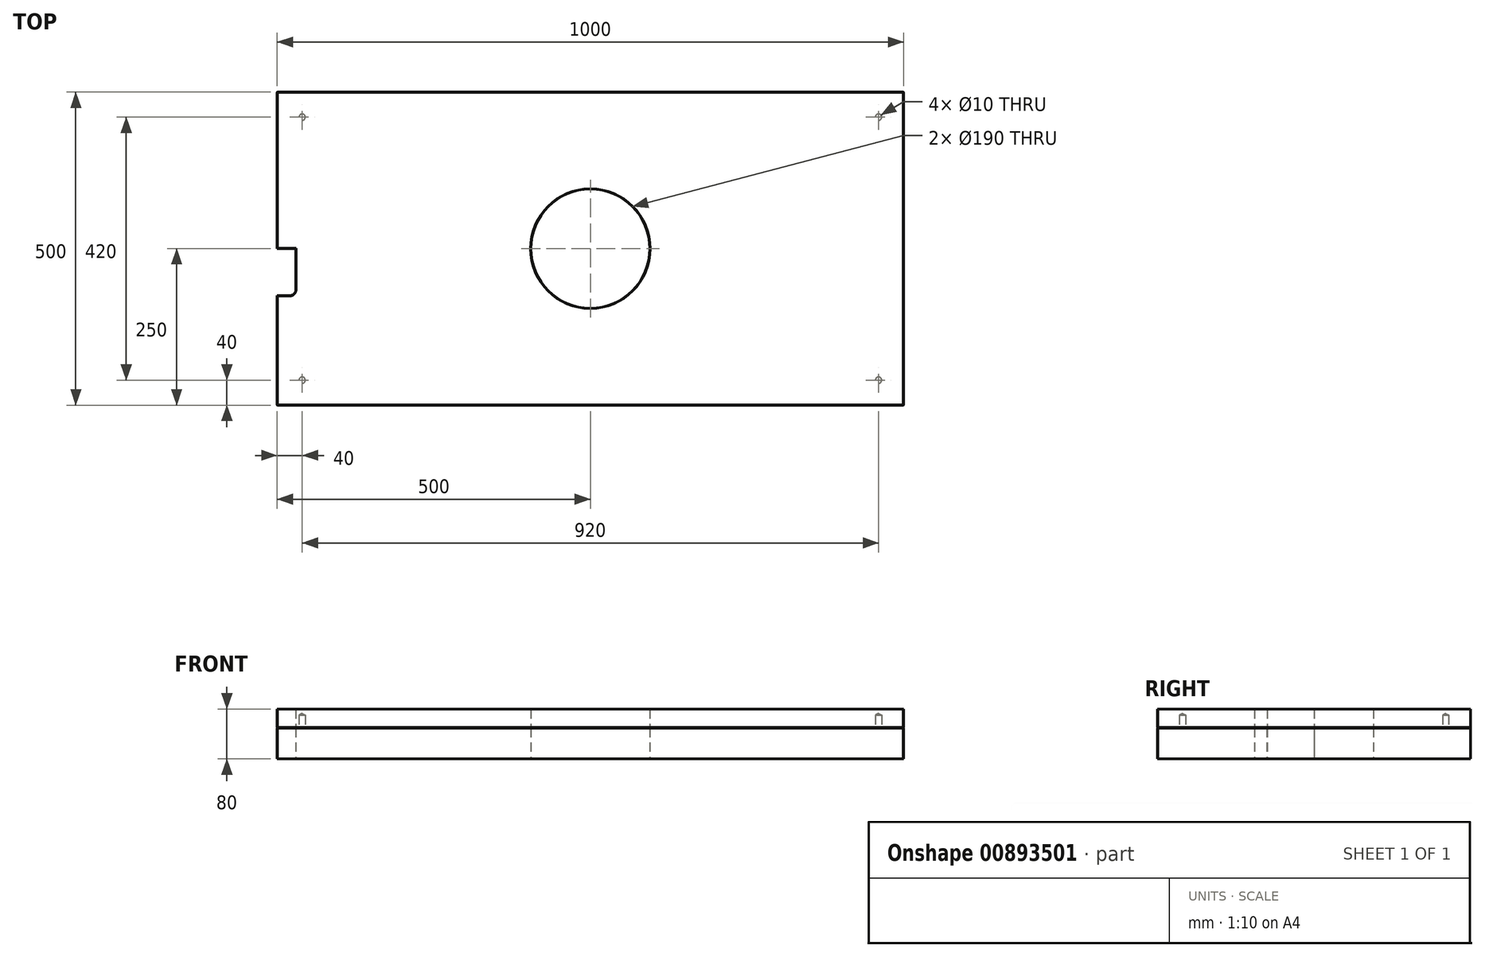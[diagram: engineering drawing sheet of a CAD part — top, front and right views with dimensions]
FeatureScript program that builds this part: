
annotation { "Feature Type Name" : "Feature", "Feature Type Description" : "" }
export const myFeature = defineFeature(function(context is Context, id is Id, definition is map)
    precondition{}
    {
        {
            var Q0;
            Q0=qCreatedBy(makeId("Top.planeOp"),FACE);
            var sketch = newSketch(context, id + "F0", { "sketchPlane" : qUnion([Q0])});
            skLineSegment(sketch, "E0", {"start": v(-650, 0) * mm, "end": v(350, 0) * mm, "construction": true});
            skLineSegment(sketch, "E1.bottom", {"start": v(350, 75) * mm, "end": v(330, 75) * mm});
            skLineSegment(sketch, "E1.top", {"start": v(350, -75) * mm, "end": v(330, -75) * mm});
            skLineSegment(sketch, "E1.left", {"start": v(350, 75) * mm, "end": v(350, -75) * mm});
            skLineSegment(sketch, "E1.right", {"start": v(320, 65) * mm, "end": v(320, -65) * mm});
            skPoint(sketch, "E2.visualSharp", {"position": v(320, -75) * mm});
            skArc(sketch, "E2.filletArc", {"start": v(320, -65) * mm, "mid": v(322.93, -72.07) * mm, "end": v(330, -75) * mm});
            skPoint(sketch, "E3.visualSharp", {"position": v(320, 75) * mm});
            skArc(sketch, "E3.filletArc", {"start": v(330, 75) * mm, "mid": v(322.93, 72.07) * mm, "end": v(320, 65) * mm});
            skLineSegment(sketch, "E4", {"start": v(-150, 250) * mm, "end": v(-150, -250) * mm, "construction": true});
            skLineSegment(sketch, "E5.MirrorCS", {"start": v(-650, 75) * mm, "end": v(-630, 75) * mm});
            skLineSegment(sketch, "E6.MirrorCS", {"start": v(-620, 65) * mm, "end": v(-620, -65) * mm});
            skArc(sketch, "E7.MirrorCS", {"start": v(-620, -65) * mm, "mid": v(-622.93, -72.07) * mm, "end": v(-630, -75) * mm});
            skArc(sketch, "E8.MirrorCS", {"start": v(-630, 75) * mm, "mid": v(-622.93, 72.07) * mm, "end": v(-620, 65) * mm});
            skLineSegment(sketch, "E9.MirrorCS", {"start": v(-650, -75) * mm, "end": v(-630, -75) * mm});
            skPoint(sketch, "E10", {"position": v(-610, 210) * mm});
            skPoint(sketch, "E11", {"position": v(310, 210) * mm});
            skPoint(sketch, "E12", {"position": v(310, -210) * mm});
            skPoint(sketch, "E13", {"position": v(-610, -210) * mm});
            skLineSegment(sketch, "E14", {"start": v(-620, 0) * mm, "end": v(-650, 0) * mm});
            skLineSegment(sketch, "E15.bottom", {"start": v(350, 250) * mm, "end": v(-650, 250) * mm});
            skLineSegment(sketch, "E15.top", {"start": v(350, -250) * mm, "end": v(-650, -250) * mm});
            skLineSegment(sketch, "E15.left", {"start": v(350, 250) * mm, "end": v(350, -250) * mm});
            skLineSegment(sketch, "E15.right", {"start": v(-650, 250) * mm, "end": v(-650, -250) * mm});
            skPoint(sketch, "E15.middle", {"position": v(-150, 0) * mm});
            skCircle(sketch, "E16", {"center": v(-150, 0) * mm, "radius": 95 * mm});
            skSolve(sketch);
        }
        {
            var Q0;
            Q0=makeQuery(id+"F0.imprint","IMPRINT",FACE,{"disambiguationData":[TD([[makeQuery(id+"F0.imprint","IMPRINT",EDGE,{"derivedFrom":sQuery(id+"F0.wireOp",EDGE,"9696f999-dd8b-4db2-95aa-c8651f8d9f2f.bottom")}),1.0]])]});
            var Q1;
            {var subQ5=sQuery(id+"F0.wireOp",EDGE,"E1.bottom");Q1=makeQuery(id+"F0.imprint","IMPRINT",FACE,{"disambiguationData":[TD([[makeQuery(id+"F0.imprint","IMPRINT",EDGE,{"derivedFrom":subQ5}),-1.0]])]});}
            var Q2;
            {var subQ1=sQuery(id+"F0.wireOp",EDGE,"E1.bottom");Q2=makeQuery(id+"F0.imprint","IMPRINT",FACE,{"disambiguationData":[TD([[makeQuery(id+"F0.imprint","IMPRINT",EDGE,{"derivedFrom":subQ1}),1.0]])]});}
            var Q3;
            {var subQ2=sQuery(id+"F0.wireOp",EDGE,"E7.MirrorCS");Q3=makeQuery(id+"F0.imprint","IMPRINT",FACE,{"disambiguationData":[TD([[makeQuery(id+"F0.imprint","IMPRINT",EDGE,{"derivedFrom":subQ2}),-1.0]])]});}
            var Q4;
            {var subQ3=sQuery(id+"F0.wireOp",EDGE,"E5.MirrorCS");Q4=makeQuery(id+"F0.imprint","IMPRINT",FACE,{"disambiguationData":[TD([[makeQuery(id+"F0.imprint","IMPRINT",EDGE,{"derivedFrom":subQ3}),-1.0]])]});}
            extrude(context, id + "F1", {"entities" : qUnion([Q0, Q1, Q2, Q3, Q4]), "depth" : 50 * mm, "offsetDistance" : 25 * mm});
        }
        {
            var Q0;
            Q0=makeQuery(id+"F1.opExtrude","CAP_FACE",FACE,{"disambiguationData":[OSD([sQuery(id+"F0.wireOp",EDGE,"E15.bottom"),sQuery(id+"F0.wireOp",EDGE,"E15.top"),sQuery(id+"F0.wireOp",EDGE,"E15.left"),sQuery(id+"F0.wireOp",EDGE,"E15.right")])],"isStart":false});
            var sketch = newSketch(context, id + "F2", { "sketchPlane" : qUnion([Q0])});
            skLineSegment(sketch, "E17.0", {"start": v(350, -75) * mm, "end": v(330, -75) * mm});
            skArc(sketch, "E18.0", {"start": v(320, -65) * mm, "mid": v(322.93, -72.07) * mm, "end": v(330, -75) * mm});
            skLineSegment(sketch, "E19.0", {"start": v(320, 65) * mm, "end": v(320, -65) * mm});
            skArc(sketch, "E20.0", {"start": v(330, 75) * mm, "mid": v(322.93, 72.07) * mm, "end": v(320, 65) * mm});
            skLineSegment(sketch, "E21.0", {"start": v(350, 75) * mm, "end": v(330, 75) * mm});
            skLineSegment(sketch, "E22.0", {"start": v(-650, -75) * mm, "end": v(-630, -75) * mm});
            skArc(sketch, "E23.0", {"start": v(-620, -65) * mm, "mid": v(-622.93, -72.07) * mm, "end": v(-630, -75) * mm});
            skLineSegment(sketch, "E24.0", {"start": v(-620, 65) * mm, "end": v(-620, -65) * mm});
            skArc(sketch, "E25.0", {"start": v(-630, 75) * mm, "mid": v(-622.93, 72.07) * mm, "end": v(-620, 65) * mm});
            skLineSegment(sketch, "E26.0", {"start": v(-650, 75) * mm, "end": v(-630, 75) * mm});
            skSolve(sketch);
        }
        {
            var Q0;
            Q0=makeQuery(id+"F1.opExtrude","CAP_FACE",FACE,{"disambiguationData":[OSD([sQuery(id+"F0.wireOp",EDGE,"E1.bottom"),sQuery(id+"F0.wireOp",EDGE,"E1.top"),sQuery(id+"F0.wireOp",EDGE,"E1.right"),sQuery(id+"F0.wireOp",EDGE,"E2.filletArc"),sQuery(id+"F0.wireOp",EDGE,"E3.filletArc"),sQuery(id+"F0.wireOp",EDGE,"E5.MirrorCS"),sQuery(id+"F0.wireOp",EDGE,"E6.MirrorCS"),sQuery(id+"F0.wireOp",EDGE,"E7.MirrorCS"),sQuery(id+"F0.wireOp",EDGE,"E8.MirrorCS"),sQuery(id+"F0.wireOp",EDGE,"E9.MirrorCS"),sQuery(id+"F0.wireOp",EDGE,"E15.bottom"),sQuery(id+"F0.wireOp",EDGE,"E15.top"),sQuery(id+"F0.wireOp",EDGE,"E15.left"),sQuery(id+"F0.wireOp",EDGE,"E15.right")])],"isStart":false});
            var sketch = newSketch(context, id + "F3", { "sketchPlane" : qUnion([Q0])});
            skLineSegment(sketch, "E27.bottom", {"start": v(-650, 250) * mm, "end": v(350, 250) * mm});
            skLineSegment(sketch, "E27.top", {"start": v(-650, -250) * mm, "end": v(350, -250) * mm});
            skLineSegment(sketch, "E27.left", {"start": v(-650, 250) * mm, "end": v(-650, -250) * mm});
            skLineSegment(sketch, "E27.right", {"start": v(350, 250) * mm, "end": v(350, -250) * mm});
            skLineSegment(sketch, "E28.0", {"start": v(-610, 210) * mm, "end": v(310, 210) * mm});
            skLineSegment(sketch, "E28.1", {"start": v(-610, 210) * mm, "end": v(-610, -210) * mm});
            skLineSegment(sketch, "E28.2", {"start": v(-610, -210) * mm, "end": v(310, -210) * mm});
            skLineSegment(sketch, "E28.3", {"start": v(310, 210) * mm, "end": v(310, -210) * mm});
            skSolve(sketch);
        }
        {
            var Q0;
            {var subQ1=makeQuery(id+"F1.opExtrude","CAP_EDGE",EDGE,{"disambiguationData":[OSD([sQuery(id+"F0.wireOp",EDGE,"E1.bottom")])],"isStart":false});Q0=makeQuery(id+"F3.imprint","IMPRINT",FACE,{"disambiguationData":[TD([[makeQuery(id+"F3.imprint","IMPRINT",EDGE,{"derivedFrom":subQ1}),1.0]])]});}
            var Q1;
            {var subQ4=sQuery(id+"F3.wireOp",EDGE,"E27.bottom");Q1=makeQuery(id+"F3.imprint","IMPRINT",FACE,{"disambiguationData":[TD([[makeQuery(id+"F3.imprint","IMPRINT",EDGE,{"derivedFrom":subQ4}),1.0]])]});}
            var Q2;
            {var subQ0=makeQuery(id+"F1.opExtrude","CAP_EDGE",EDGE,{"disambiguationData":[OSD([sQuery(id+"F0.wireOp",EDGE,"E5.MirrorCS")])],"isStart":false});Q2=makeQuery(id+"F3.imprint","IMPRINT",FACE,{"disambiguationData":[TD([[makeQuery(id+"F3.imprint","IMPRINT",EDGE,{"derivedFrom":subQ0}),-1.0]])]});}
            var Q3;
            Q3=makeQuery(id+"F3.imprint","IMPRINT",FACE,{"disambiguationData":[TD([[makeQuery(id+"F3.imprint","IMPRINT",EDGE,{"derivedFrom":sQuery(id+"F3.wireOp",EDGE,"E28.0")}),-1.0]])]});
            var Q4;
            {var subQ4=sQuery(id+"F3.wireOp",EDGE,"E27.bottom");Q4=makeQuery(id+"F3.imprint","IMPRINT",FACE,{"disambiguationData":[TD([[makeQuery(id+"F3.imprint","IMPRINT",EDGE,{"derivedFrom":subQ4}),1.0]])]});}
            var Q5;
            Q5=makeQuery(id+"F3.imprint","IMPRINT",FACE,{"disambiguationData":[TD([[makeQuery(id+"F3.imprint","IMPRINT",EDGE,{"derivedFrom":sQuery(id+"F3.wireOp",EDGE,"E28.0")}),-1.0]])]});
            var Q6;
            {var subQ0=makeQuery(id+"FIPpv0qjfYkindW_1.boolean.opBoolean","COPY",EDGE,{"derivedFrom":makeQuery(id+"FIPpv0qjfYkindW_1.opExtrude","CAP_EDGE",EDGE,{"disambiguationData":[OSD([sQuery(id+"F2.wireOp",EDGE,"E17.0")])],"isStart":true})});Q6=makeQuery(id+"F3.imprint","IMPRINT",FACE,{"disambiguationData":[TD([[makeQuery(id+"F3.imprint","IMPRINT",EDGE,{"derivedFrom":subQ0}),-1.0]])]});}
            var Q7;
            {var subQ0=makeQuery(id+"FIPpv0qjfYkindW_1.boolean.opBoolean","COPY",EDGE,{"derivedFrom":makeQuery(id+"FIPpv0qjfYkindW_1.opExtrude","CAP_EDGE",EDGE,{"disambiguationData":[OSD([sQuery(id+"F2.wireOp",EDGE,"E22.0")])],"isStart":true})});Q7=makeQuery(id+"F3.imprint","IMPRINT",FACE,{"disambiguationData":[TD([[makeQuery(id+"F3.imprint","IMPRINT",EDGE,{"derivedFrom":subQ0}),1.0]])]});}
            extrude(context, id + "F4", {"entities" : qUnion([Q0, Q1, Q2, Q3, Q4, Q5, Q6, Q7]), "depth" : 30 * mm});
        }
        {
            var Q0;
            Q0=makeQuery(id+"F4.opExtrude","CAP_FACE",FACE,{"disambiguationData":[OSD([sQuery(id+"F3.wireOp",EDGE,"E27.bottom"),sQuery(id+"F3.wireOp",EDGE,"E27.top"),sQuery(id+"F3.wireOp",EDGE,"E27.left"),sQuery(id+"F3.wireOp",EDGE,"E27.right")])],"isStart":false});
            var Q1;
            Q1=makeQuery(id+"F4.opExtrude","CAP_FACE",FACE,{"disambiguationData":[OSD([sQuery(id+"F3.wireOp",EDGE,"E27.bottom"),sQuery(id+"F3.wireOp",EDGE,"E27.top"),sQuery(id+"F3.wireOp",EDGE,"E27.left"),sQuery(id+"F3.wireOp",EDGE,"E27.right")])],"isStart":true});
            var Q2;
            Q2=makeQuery(id+"F4.opExtrude","SWEPT_EDGE",EDGE,{"disambiguationData":[OSD([sQuery(id+"F3.wireOp",EDGE,"E27.bottom"),sQuery(id+"F3.wireOp",EDGE,"E27.right")])]});
            var Q3;
            Q3=makeQuery(id+"F4.opExtrude","SWEPT_EDGE",EDGE,{"disambiguationData":[OSD([sQuery(id+"F3.wireOp",EDGE,"E27.bottom"),sQuery(id+"F3.wireOp",EDGE,"E27.left")])]});
            var Q4;
            Q4=makeQuery(id+"F4.opExtrude","SWEPT_EDGE",EDGE,{"disambiguationData":[OSD([sQuery(id+"F3.wireOp",EDGE,"E27.top"),sQuery(id+"F3.wireOp",EDGE,"E27.left")])]});
            var Q5;
            Q5=makeQuery(id+"F4.opExtrude","SWEPT_EDGE",EDGE,{"disambiguationData":[OSD([sQuery(id+"F3.wireOp",EDGE,"E27.top"),sQuery(id+"F3.wireOp",EDGE,"E27.right")])]});
            chamfer(context, id + "F5", {"entities" : qUnion([Q0, Q1, Q2, Q3, Q4, Q5]), "width" : 0.5 * mm, "tangentPropagation" : true});
        }
        {
            var Q0;
            Q0=sQuery(id+"F3.wireOp",VERTEX,"E28.1.start");
            var Q1;
            Q1=sQuery(id+"F3.wireOp",VERTEX,"E28.0.end");
            var Q2;
            Q2=sQuery(id+"F3.wireOp",VERTEX,"E28.3.end");
            var Q3;
            Q3=sQuery(id+"F3.wireOp",VERTEX,"E28.2.start");
            var Q4;
            Q4=makeQuery(id+"F4.opExtrude","SWEPT_BODY",BODY,{"disambiguationData":[OSD([sQuery(id+"F3.wireOp",EDGE,"E27.bottom"),sQuery(id+"F3.wireOp",EDGE,"E27.top"),sQuery(id+"F3.wireOp",EDGE,"E27.left"),sQuery(id+"F3.wireOp",EDGE,"E27.right")])]});
            hole(context, id + "F6", {"style" : HoleStyle.SIMPLE, "endStyle" : HoleEndStyle.BLIND, "oppositeDirection" : true, "holeDiameter" : 10 * mm, "holeDepth" : 20 * mm, "isTappedThrough" : true, "tappedDepth" : 12 * mm, "tapClearance" : 3, "locations" : qUnion([Q0, Q1, Q2, Q3]), "scope" : qUnion([Q4])});
        }
        {
            var Q0;
            Q0=makeQuery(id+"F1.opExtrude","CAP_FACE",FACE,{"disambiguationData":[OSD([sQuery(id+"F0.wireOp",EDGE,"E1.bottom"),sQuery(id+"F0.wireOp",EDGE,"E1.top"),sQuery(id+"F0.wireOp",EDGE,"E1.right"),sQuery(id+"F0.wireOp",EDGE,"E2.filletArc"),sQuery(id+"F0.wireOp",EDGE,"E3.filletArc"),sQuery(id+"F0.wireOp",EDGE,"E5.MirrorCS"),sQuery(id+"F0.wireOp",EDGE,"E6.MirrorCS"),sQuery(id+"F0.wireOp",EDGE,"E7.MirrorCS"),sQuery(id+"F0.wireOp",EDGE,"E8.MirrorCS"),sQuery(id+"F0.wireOp",EDGE,"E9.MirrorCS"),sQuery(id+"F0.wireOp",EDGE,"E15.bottom"),sQuery(id+"F0.wireOp",EDGE,"E15.top"),sQuery(id+"F0.wireOp",EDGE,"E15.left"),sQuery(id+"F0.wireOp",EDGE,"E15.right")])],"isStart":false});
            var Q1;
            {var subQ0=sQuery(id+"F0.wireOp",EDGE,"E15.right");var subQ1=sQuery(id+"F0.wireOp",EDGE,"E15.left");var subQ2=sQuery(id+"F0.wireOp",EDGE,"E15.top");var subQ3=sQuery(id+"F0.wireOp",EDGE,"E15.bottom");Q1=makeQuery(id+"FSn3DBmeKnvXifK_2.boolean.opBoolean","MERGE",FACE,{"derivedFrom":[makeQuery(id+"F1.opExtrude","CAP_FACE",FACE,{"disambiguationData":[OSD([sQuery(id+"F0.wireOp",EDGE,"E1.bottom"),sQuery(id+"F0.wireOp",EDGE,"E1.top"),sQuery(id+"F0.wireOp",EDGE,"E1.right"),sQuery(id+"F0.wireOp",EDGE,"E2.filletArc"),sQuery(id+"F0.wireOp",EDGE,"E3.filletArc"),sQuery(id+"F0.wireOp",EDGE,"E5.MirrorCS"),sQuery(id+"F0.wireOp",EDGE,"E6.MirrorCS"),sQuery(id+"F0.wireOp",EDGE,"E7.MirrorCS"),sQuery(id+"F0.wireOp",EDGE,"E8.MirrorCS"),sQuery(id+"F0.wireOp",EDGE,"E9.MirrorCS"),subQ3,subQ2,subQ1,subQ0])],"isStart":true}),makeQuery(id+"FSn3DBmeKnvXifK_2.opExtrude","CAP_FACE",FACE,{"disambiguationData":[OSD([subQ3,subQ2,subQ1,subQ0])],"isStart":true})]});}
            var Q2;
            Q2=makeQuery(id+"F1.opExtrude","SWEPT_FACE",FACE,{"disambiguationData":[OSD([sQuery(id+"F0.wireOp",EDGE,"E15.top")])]});
            var Q3;
            {var subQ0=sQuery(id+"F0.wireOp",EDGE,"E15.left");Q3=makeQuery(id+"FSn3DBmeKnvXifK_2.boolean.opBoolean","MERGE",FACE,{"derivedFrom":[makeQuery(id+"F1.opExtrude","SWEPT_FACE",FACE,{"disambiguationData":[OSD([subQ0]),TDD([makeQuery(id+"F0.imprint","IMPRINT",EDGE,{"disambiguationData":[TD([[makeQuery(id+"F0.imprint","INTERSECT",VERTEX,{"derivedFrom":[sQuery(id+"F0.wireOp",EDGE,"E1.bottom"),subQ0]}),1.0]])],"derivedFrom":subQ0})])]}),makeQuery(id+"F1.opExtrude","SWEPT_FACE",FACE,{"disambiguationData":[OSD([subQ0]),TDD([makeQuery(id+"F0.imprint","IMPRINT",EDGE,{"disambiguationData":[TD([[makeQuery(id+"F0.imprint","INTERSECT",VERTEX,{"derivedFrom":[sQuery(id+"F0.wireOp",EDGE,"E1.top"),subQ0]}),-1.0]])],"derivedFrom":subQ0})])]}),makeQuery(id+"FSn3DBmeKnvXifK_2.opExtrude","SWEPT_FACE",FACE,{"disambiguationData":[OSD([subQ0])]})]});}
            var Q4;
            {var subQ0=sQuery(id+"F0.wireOp",EDGE,"E15.right");Q4=makeQuery(id+"FSn3DBmeKnvXifK_2.boolean.opBoolean","MERGE",FACE,{"derivedFrom":[makeQuery(id+"F1.opExtrude","SWEPT_FACE",FACE,{"disambiguationData":[OSD([subQ0]),TDD([makeQuery(id+"F0.imprint","IMPRINT",EDGE,{"disambiguationData":[TD([[makeQuery(id+"F0.imprint","INTERSECT",VERTEX,{"derivedFrom":[sQuery(id+"F0.wireOp",EDGE,"E5.MirrorCS"),subQ0]}),1.0]])],"derivedFrom":subQ0})])]}),makeQuery(id+"F1.opExtrude","SWEPT_FACE",FACE,{"disambiguationData":[OSD([subQ0]),TDD([makeQuery(id+"F0.imprint","IMPRINT",EDGE,{"disambiguationData":[TD([[makeQuery(id+"F0.imprint","INTERSECT",VERTEX,{"derivedFrom":[sQuery(id+"F0.wireOp",EDGE,"E9.MirrorCS"),subQ0]}),-1.0]])],"derivedFrom":subQ0})])]}),makeQuery(id+"FSn3DBmeKnvXifK_2.opExtrude","SWEPT_FACE",FACE,{"disambiguationData":[OSD([subQ0])]})]});}
            var Q5;
            Q5=makeQuery(id+"F1.opExtrude","SWEPT_FACE",FACE,{"disambiguationData":[OSD([sQuery(id+"F0.wireOp",EDGE,"E15.bottom")])]});
            var Q6;
            {var subQ0=sQuery(id+"F0.wireOp",EDGE,"E16");Q6=makeQuery(id+"F5.opChamfer","BLEND_EDGE",EDGE,{"blendedFrom":[makeQuery(id+"F4.opExtrude","CAP_EDGE",EDGE,{"disambiguationData":[OSD([subQ0])],"isStart":false}),makeQuery(id+"F4.opExtrude","SWEPT_FACE",FACE,{"disambiguationData":[OSD([subQ0])]})],"blendedInto":[makeQuery(id+"F4.opExtrude","SWEPT_FACE",FACE,{"disambiguationData":[OSD([subQ0])]})]});}
            chamfer(context, id + "F7", {"entities" : qUnion([Q0, Q1, Q2, Q3, Q4, Q5, Q6]), "width" : 0.5 * mm, "tangentPropagation" : true});
        }
    });
